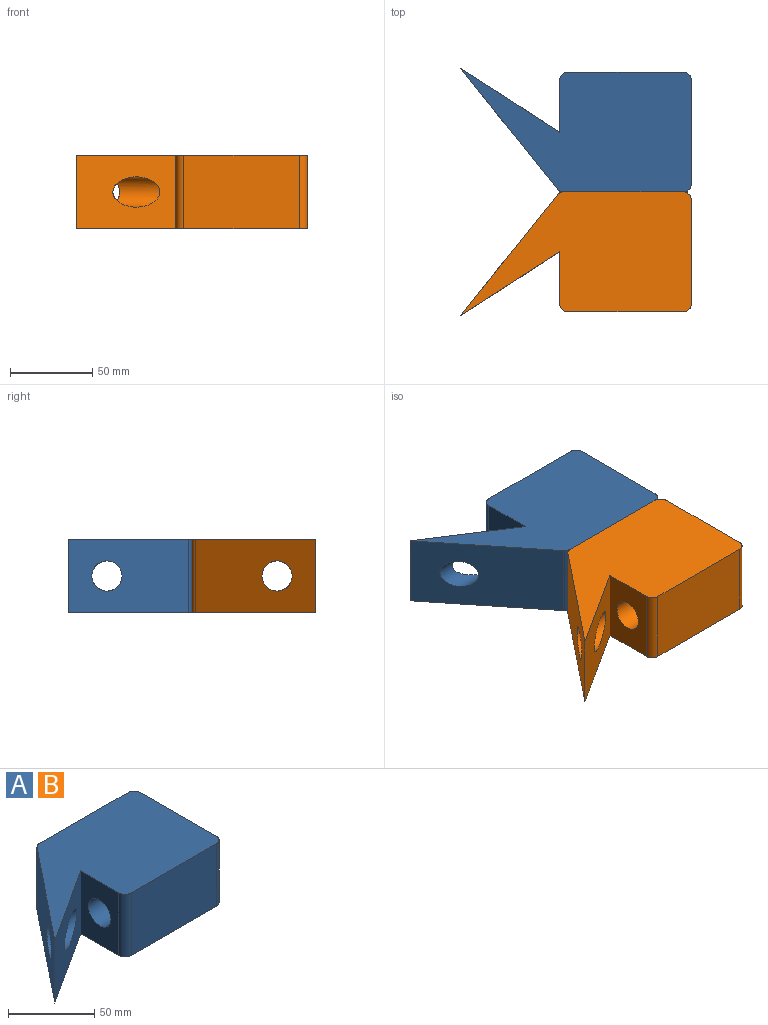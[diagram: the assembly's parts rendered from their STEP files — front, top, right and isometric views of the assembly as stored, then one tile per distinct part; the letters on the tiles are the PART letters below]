
ASSEMBLY  parts=2 mates=1
PART A: 14 faces, bbox 140.1x75x44.5 mm
  f0: plane 72.6x44.5mm, normal (0,1,0), area 3230.6mm2, adj f6,f7,f8,f9
  f1: plane 73.12x58.55mm, normal (-0.78,0.63,0), area 3830.5mm2, adj f2,f6,f7,f9,f13
  f2: plane 60.05x44.5mm, normal (0.54,-0.84,0), area 2693.4mm2, adj f1,f3,f6,f7,f13
  f3: plane 44.5x31.26mm, normal (-1,0,0), area 1127.2mm2, adj f2,f6,f7,f10,f12
  f4: plane 70x44.5mm, normal (0,-1,0), area 3115mm2, adj f6,f7,f10,f11
  f5: plane 62.52x44.5mm, normal (1,0,0), area 2518.3mm2, adj f6,f7,f8,f11,f12
  f6: plane 140.05x74.99mm, normal (0,0,1), area 6873.3mm2, adj f0,f1,f2,f3,f4,f5,f8,f9
  f7: plane 140.05x74.99mm, normal (0,0,-1), area 6873.3mm2, adj f0,f1,f2,f3,f4,f5,f8,f9
  f8: cylinder r=5mm len=44.5mm, axis (0,0,-1), area 349.5mm2, adj f0,f5,f6,f7
  f9: cylinder r=5mm len=44.5mm, axis (0,0,-1), area 199.3mm2, adj f0,f1,f6,f7
  f10: cylinder r=5mm len=44.5mm, axis (0,0,-1), area 349.5mm2, adj f3,f4,f6,f7
  f11: cylinder r=5mm len=44.5mm, axis (0,0,1), area 349.5mm2, adj f4,f5,f6,f7
  f12: cylinder r=9.16mm len=80mm, axis (1,0,0), area 4606mm2, adj f3,f5
  f13: cylinder r=9.16mm len=39.21mm, axis (1,0,0), area 1010.6mm2, adj f1,f2
PART B: same geometry as A
PLACE A rot(axis=(1,0,0),180deg) t=(31.14,126.71,21.66)mm
PLACE B t=(31.14,-51.32,-22.84)mm
MATE fastened A.f0 <-> B.f0  axis (0,-1,0) through (29.76,37.7,-0.59)mm
